# Revit family: ONRZ 5.125'' - Heated Only-All
name_source: partatom
category: Mechanical Equipment
units: mm (PartAtom-declared; Revit-internal decimal feet)

## family parameters
Always vertical = Yes
Cut with Voids When Loaded = No
OmniClass Number = 23.40.40.11.17
OmniClass Title = Refrigerated Cases
Part Type = Normal
Room Calculation Point = No
Round Connector Dimension = Use Radius
Shared = No
Work Plane-Based = Yes

## types (6) — shared parameters
20" Shelf = Yes
22" Shelf = Yes
Application Discipline = Frozen
Certifications = NSF 7, UL471, CSA
DATE = 02/04/2016
DESIGNERS NAME = SHIDDRAMESH
DRAIN LINE CONNECTION = SANITARY LINE CONNECTION
DRAIN LINE DIAMETER = 2"
DRAIN PIPE TYPE = PVC
DRIP PAN PLUMB TYPE = HARD
Default Elevation = 48"
Defrost Num Day = 1
Defrost Type = ELECTRIC DEFROST
Defrosts Per Day_2 = 1
Description = Narrow Reach-In Merchandiser
Discharge Air (°F) = -1° F
Discharge Air Velocity (FPM) = 350 (FPM)
EQUIPMENT DESCRIPTION = Narrow Reach-In Merchandiser
EQUIPMENT MARK = ONRZ
Electric Defrost Fail-Safe = 46 (Min)
Electric Defrost Run-Off Time (Min) = 0 (Min)
Electric Defrost Termination Temp (°F) = 50° F
Evap Temp = -15
Evaporator (°F) = -7° F
GLASS = Glass
Heated/Low E = Heated
Height = 81 1/4"
Hot Gas Defrost Fail-Safe = 24 (Min)
Hot Gas Defrost Run-Off Time (Min) = 13-15 (Min)
Hot Gas Defrost Termination = 73° F
Item Description = Narrow Reach-In Merchandiser
Keynote = ONRZ
LIQUID LINE CONNECTION = LIQUID LINE CONNECTION
LIQUID LINE DIAMETER = 0"
LIQUID LINE RADIUS = 0"
Legend Number = ONRZ
Load Mbh = 1.06
Manufacturer = HILL PHOENIX
Model = ONRZ
PAINTED METAL UPPER SHELF = PAINTED SHELVES
PRESSURE REGULATOR = 0.00 psi
REFRIGERATION PIPING = COPPER PIPE
Refrig Charge Lbs = 0
SANITARY PIPE SIZE = 1"
STAINLESS STEEL = GALVANIZED STEEL
SUCTION LINE CONNECTION = SUCTION LINE CONNECTION
SUCTION LINE DIAMETER = 1"
SUCTION LINE RADIUS = 0"
Size of Door = 30"
Superheat Set Point @ Bulb (°F) = 3-5° F
URL = http://www.hillphoenix.com
Width = 34 5/8"

## per-type parameters (varying)
- 2 Door - Frozen - Heated: BTUH Conventional=1044; BTUH Parallel=1014; CENTER LINE & DRAIN=30"; Combined Heated Rails Amps=2 A; Combined Heated Rails Watts=206 W; Combined Low E Rails Amps=2 A; Combined Low E Rails Watts=181 W; DISCHARGE AIR TEMP.=-8 °F; DISCHARGE AIR VELOCITY=350 FPM; DOOR CONFIGURATION=MASTER DOOR : 30" X 64 3/8" 2 DOOR A SWING (LEFT OPENING); Defrost (Phase 1) 208 V Amps=8 A; Defrost (Phase 1) 208 V Watts=1552 W; Defrost (Phase 1) 240 V Amps=9 A; Defrost (Phase 1) 240 V Watts=2068 W; Defrost (Phase 3) 208 V Amps=7 A; Defrost (Phase 3) 208 V Watts=1552 W; Defrost (Phase 3) 240 V Amps=8 A; Defrost (Phase 3) 240 V Watts=2068 W; Defrost Termination=50 °F; GE Immersion Amps=0 A; GE Immersion Watts=41 W; High Efficiency Amps=1 A; High Efficiency Watts=50 W; Individual 101-LE Frame Amps=1 A; Individual 101-LE Frame Watts=143 W; Individual Heated Doors Amps=1 A; Individual Heated Doors Watts=63 W; Individual Low E Doors Amps=0 A; Individual Low E Doors Watts=38 W; Length=60"; Length of Cases=60"; NUMBER OF DOORS=2; Number of Fans=2; Optimax Pro Amps=0 A; Optimax Pro Watts=43 W; Tank/Drain Heater Amps=1 A; Tank/Drain Heater Watts=152 W; Type of Door Swing=B-Swing
- 3 Door - Frozen - Heated: BTUH Conventional=892; BTUH Parallel=850; CENTER LINE & DRAIN=45"; Combined Heated Rails Amps=3 A; Combined Heated Rails Watts=295 W; Combined Low E Rails Amps=2 A; Combined Low E Rails Watts=258 W; DISCHARGE AIR TEMP.=-8 °F; DISCHARGE AIR VELOCITY=350 FPM; DOOR CONFIGURATION=MASTER DOOR : 30" X 64 3/8" 3 DOOR A SWING (LEFT OPENING); Defrost (Phase 1) 208 V Amps=11 A; Defrost (Phase 1) 208 V Watts=2274 W; Defrost (Phase 1) 240 V Amps=13 A; Defrost (Phase 1) 240 V Watts=3018 W; Defrost (Phase 3) 208 V Amps=10 A; Defrost (Phase 3) 208 V Watts=2274 W; Defrost (Phase 3) 240 V Amps=11 A; Defrost (Phase 3) 240 V Watts=3018 W; Defrost Termination=50 °F; GE Immersion Amps=0 A; GE Immersion Watts=48 W; High Efficiency Amps=1 A; High Efficiency Watts=75 W; Individual 101-LE Frame Amps=2 A; Individual 101-LE Frame Watts=200 W; Individual Heated Doors Amps=1 A; Individual Heated Doors Watts=95 W; Individual Low E Doors Amps=0 A; Individual Low E Doors Watts=58 W; Length=90"; Length of Cases=90"; NUMBER OF DOORS=3; Number of Fans=3; Optimax Pro Amps=1 A; Optimax Pro Watts=65 W; Tank/Drain Heater Amps=2 A; Tank/Drain Heater Watts=171 W; Type of Door Swing=A-Swing
- 5 Door - Frozen - Heated: BTUH Conventional=1044; BTUH Parallel=1014; CENTER LINE & DRAIN=75"; Combined Heated Rails Amps=4 A; Combined Heated Rails Watts=475 W; Combined Low E Rails Amps=3 A; Combined Low E Rails Watts=413 W; DISCHARGE AIR TEMP.=-8 °F; DISCHARGE AIR VELOCITY=350 FPM; DOOR CONFIGURATION=MASTER DOOR : 30" X 64 3/8" 5 DOOR A SWING (LEFT OPENING); Defrost (Phase 1) 208 V Amps=18 A; Defrost (Phase 1) 208 V Watts=3640 W; Defrost (Phase 1) 240 V Amps=20 A; Defrost (Phase 1) 240 V Watts=4840 W; Defrost (Phase 3) 208 V Amps=15 A; Defrost (Phase 3) 208 V Watts=3640 W; Defrost (Phase 3) 240 V Amps=17 A; Defrost (Phase 3) 240 V Watts=4840 W; Defrost Termination=50 °F; GE Immersion Amps=1 A; GE Immersion Watts=80 W; High Efficiency Amps=2 A; High Efficiency Watts=125 W; Individual 101-LE Frame Amps=3 A; Individual 101-LE Frame Watts=317 W; Individual Heated Doors Amps=2 A; Individual Heated Doors Watts=158 W; Individual Low E Doors Amps=1 A; Individual Low E Doors Watts=96 W; Length=150"; Length of Cases=150"; NUMBER OF DOORS=5; Number of Fans=5; Optimax Pro Amps=1 A; Optimax Pro Watts=109 W; Tank/Drain Heater Amps=2 A; Tank/Drain Heater Watts=275 W; Type of Door Swing=A-Swing
- 6 Door - Frozen - Heated: BTUH Conventional=988; BTUH Parallel=960; CENTER LINE & DRAIN=90"; Combined Heated Rails Amps=5 A; Combined Heated Rails Watts=565 W; Combined Low E Rails Amps=4 A; Combined Low E Rails Watts=491 W; DISCHARGE AIR TEMP.=-8 °F; DISCHARGE AIR VELOCITY=350 FPM; DOOR CONFIGURATION=MASTER DOOR : 30" X 64 3/8" 6 DOOR A SWING (LEFT OPENING); Defrost (Phase 1) 208 V Amps=20 A; Defrost (Phase 1) 208 V Watts=4224 W; Defrost (Phase 1) 240 V Amps=23 A; Defrost (Phase 1) 240 V Watts=5624 W; Defrost (Phase 3) 208 V Amps=18 A; Defrost (Phase 3) 208 V Watts=4224 W; Defrost (Phase 3) 240 V Amps=20 A; Defrost (Phase 3) 240 V Watts=5624 W; Defrost Termination=50 °F; GE Immersion Amps=1 A; GE Immersion Watts=96 W; High Efficiency Amps=2 A; High Efficiency Watts=150 W; Individual 101-LE Frame Amps=3 A; Individual 101-LE Frame Watts=376 W; Individual Heated Doors Amps=2 A; Individual Heated Doors Watts=190 W; Individual Low E Doors Amps=1 A; Individual Low E Doors Watts=115 W; Length=180"; Length of Cases=180"; NUMBER OF DOORS=6; Number of Fans=6; Optimax Pro Amps=1 A; Optimax Pro Watts=132 W; Tank/Drain Heater Amps=3 A; Tank/Drain Heater Watts=320 W; Type of Door Swing=B-Swing
- 1 Door: BTUH Conventional=910; BTUH Parallel=895; CENTER LINE & DRAIN=15 1/2"; Combined Heated Rails Amps=1 A; Combined Heated Rails Watts=118 W; Combined Low E Rails Amps=1 A; Combined Low E Rails Watts=105 W; DISCHARGE AIR TEMP.=-8 °F; DISCHARGE AIR VELOCITY=350 FPM; DOOR CONFIGURATION=MASTER DOOR : 31" X 64 3/8" 1 DOOR A SWING (LEFT OPENING); Defrost (Phase 1) 208 V Amps=3 A; Defrost (Phase 1) 208 V Watts=680 W; Defrost (Phase 1) 240 V Amps=4 A; Defrost (Phase 1) 240 V Watts=906 W; Defrost (Phase 3) 208 V Amps=3 A; Defrost (Phase 3) 208 V Watts=680 W; Defrost (Phase 3) 240 V Amps=3 A; Defrost (Phase 3) 240 V Watts=906 W; Defrost Termination=50 °F; GE Immersion Amps=0 A; GE Immersion Watts=27 W; High Efficiency Amps=0 A; High Efficiency Watts=25 W; Individual 101-LE Frame Amps=1 A; Individual 101-LE Frame Watts=86 W; Individual Heated Doors Amps=0 A; Individual Heated Doors Watts=32 W; Individual Low E Doors Amps=0 A; Individual Low E Doors Watts=19 W; Length=31"; Length of Cases=31"; NUMBER OF DOORS=2; Number of Fans=1; Optimax Pro Amps=0 A; Optimax Pro Watts=21 W; Tank/Drain Heater Amps=0 A; Tank/Drain Heater Watts=113 W; Type of Door Swing=A-Swing
- 4 Door - Frozen - Heated: BTUH Conventional=1044; BTUH Parallel=1014; CENTER LINE & DRAIN=60"; Combined Heated Rails Amps=4 A; Combined Heated Rails Watts=475 W; Combined Low E Rails Amps=3 A; Combined Low E Rails Watts=413 W; DISCHARGE AIR TEMP.=-8; DISCHARGE AIR VELOCITY=350; DOOR CONFIGURATION=MASTER DOOR : 30" X 64 3/8" 4 DOOR A SWING (LEFT OPENING); Defrost (Phase 1) 208 V Amps=14 A; Defrost (Phase 1) 208 V Watts=2984 W; Defrost (Phase 1) 240 V Amps=17 A; Defrost (Phase 1) 240 V Watts=3992 W; Defrost (Phase 3) 208 V Amps=12 A; Defrost (Phase 3) 208 V Watts=2984 W; Defrost (Phase 3) 240 V Amps=14 A; Defrost (Phase 3) 240 V Watts=3992 W; Defrost Termination=50; GE Immersion Amps=1 A; GE Immersion Watts=80 W; High Efficiency Amps=1 A; High Efficiency Watts=100 W; Individual 101-LE Frame Amps=3 A; Individual 101-LE Frame Watts=317 W; Individual Heated Doors Amps=2 A; Individual Heated Doors Watts=158 W; Individual Low E Doors Amps=1 A; Individual Low E Doors Watts=96 W; Length=120"; Length of Cases=120"; NUMBER OF DOORS=4; Number of Fans=4; Optimax Pro Amps=1 A; Optimax Pro Watts=87 W; Tank/Drain Heater Amps=2 A; Tank/Drain Heater Watts=226 W; Type of Door Swing=A-Swing

## geometry (parser evidence)
native form markers: Blend x10, Sweep x17
no freeform markers — native parametric forms only
